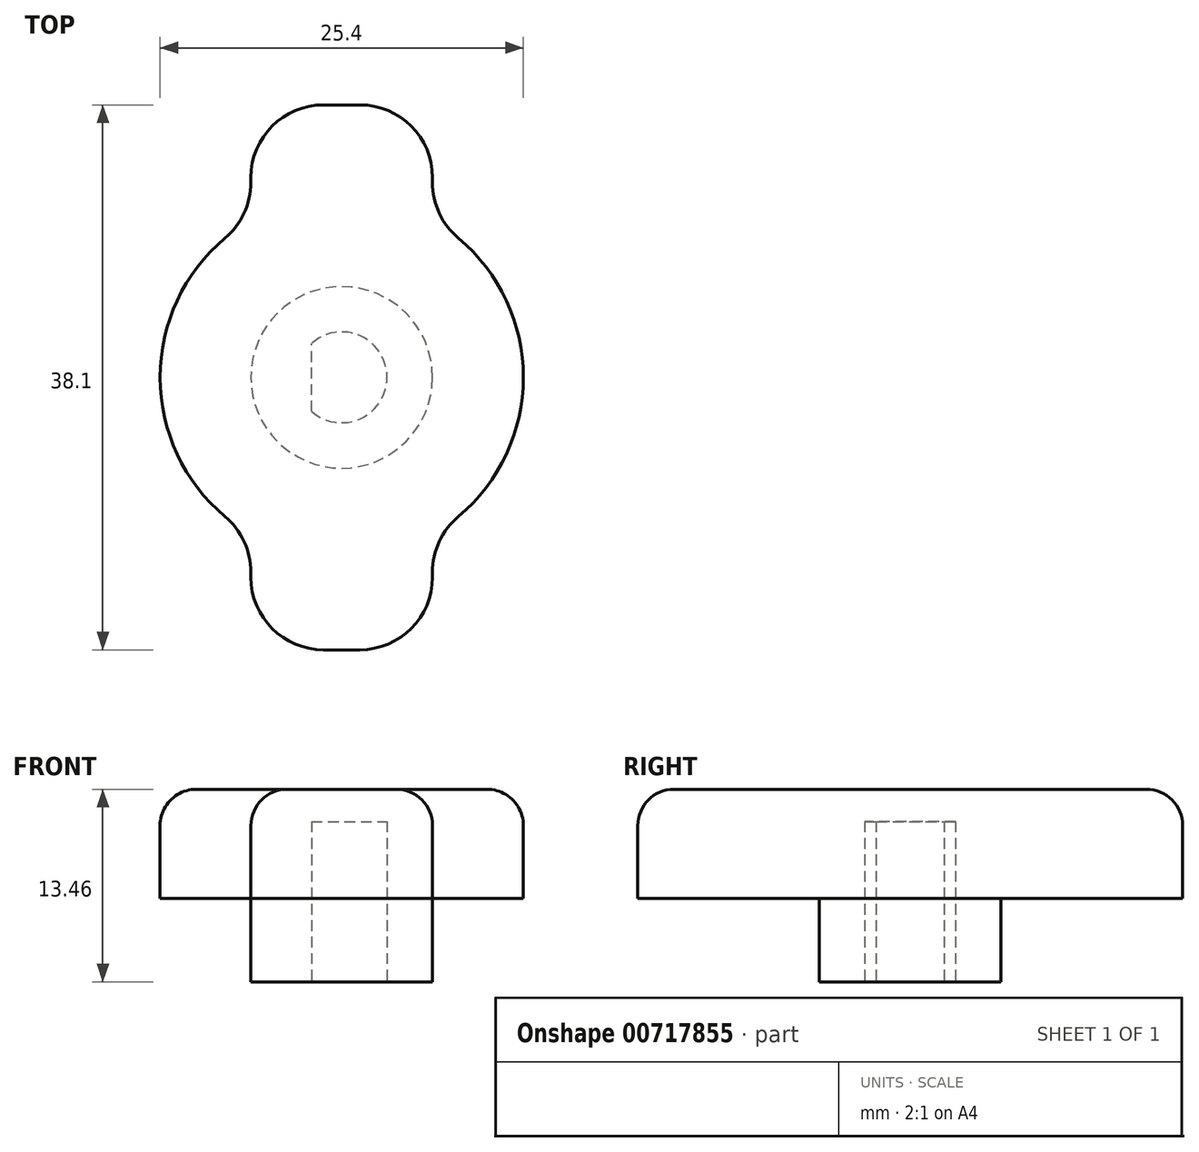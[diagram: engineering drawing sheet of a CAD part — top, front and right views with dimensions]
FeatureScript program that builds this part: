
annotation { "Feature Type Name" : "Feature", "Feature Type Description" : "" }
export const myFeature = defineFeature(function(context is Context, id is Id, definition is map)
    precondition{}
    {
        {
            var Q0;
            Q0=qCreatedBy(makeId("Top.planeOp"),FACE);
            var sketch = newSketch(context, id + "F0", { "sketchPlane" : qUnion([Q0])});
            skCircle(sketch, "E0", {"center": v(0, 0) * mm, "radius": 12.7 * mm});
            skLineSegment(sketch, "E1.bottom", {"start": v(6.35, -19.05) * mm, "end": v(-6.35, -19.05) * mm});
            skLineSegment(sketch, "E1.top", {"start": v(6.35, 19.05) * mm, "end": v(-6.35, 19.05) * mm});
            skLineSegment(sketch, "E1.left", {"start": v(6.35, -19.05) * mm, "end": v(6.35, 19.05) * mm});
            skLineSegment(sketch, "E1.right", {"start": v(-6.35, -19.05) * mm, "end": v(-6.35, 19.05) * mm});
            skSolve(sketch);
        }
        {
            var Q0;
            Q0 = qSketchRegion(id + "F0", true);
            extrude(context, id + "F1", {"entities" : qUnion([Q0]), "depth" : 7.62 * mm, "offsetDistance" : 25.4 * mm});
        }
        {
            var Q0;
            {var subQ0=sQuery(id+"F0.wireOp",EDGE,"E1.left");var subQ1=sQuery(id+"F0.wireOp",EDGE,"E0");Q0=makeQuery(id+"F1.opExtrude","SWEPT_EDGE",EDGE,{"disambiguationData":[OSD([subQ1,subQ0]),TDD([makeQuery(id+"F0.imprint","INTERSECT",VERTEX,{"disambiguationData":[OD(1.0)],"derivedFrom":[subQ1,subQ0]})])]});}
            var Q1;
            Q1=makeQuery(id+"F1.opExtrude","SWEPT_EDGE",EDGE,{"disambiguationData":[OSD([sQuery(id+"F0.wireOp",EDGE,"E1.bottom"),sQuery(id+"F0.wireOp",EDGE,"E1.left")])]});
            var Q2;
            Q2=makeQuery(id+"F1.opExtrude","SWEPT_EDGE",EDGE,{"disambiguationData":[OSD([sQuery(id+"F0.wireOp",EDGE,"E1.bottom"),sQuery(id+"F0.wireOp",EDGE,"E1.right")])]});
            var Q3;
            {var subQ0=sQuery(id+"F0.wireOp",EDGE,"E1.right");var subQ1=sQuery(id+"F0.wireOp",EDGE,"E0");Q3=makeQuery(id+"F1.opExtrude","SWEPT_EDGE",EDGE,{"disambiguationData":[OSD([subQ1,subQ0]),TDD([makeQuery(id+"F0.imprint","INTERSECT",VERTEX,{"disambiguationData":[OD(1.0)],"derivedFrom":[subQ1,subQ0]})])]});}
            var Q4;
            {var subQ0=sQuery(id+"F0.wireOp",EDGE,"E1.right");var subQ1=sQuery(id+"F0.wireOp",EDGE,"E0");Q4=makeQuery(id+"F1.opExtrude","SWEPT_EDGE",EDGE,{"disambiguationData":[OSD([subQ1,subQ0]),TDD([makeQuery(id+"F0.imprint","INTERSECT",VERTEX,{"disambiguationData":[OD(0.0)],"derivedFrom":[subQ1,subQ0]})])]});}
            var Q5;
            Q5=makeQuery(id+"F1.opExtrude","SWEPT_EDGE",EDGE,{"disambiguationData":[OSD([sQuery(id+"F0.wireOp",EDGE,"E1.top"),sQuery(id+"F0.wireOp",EDGE,"E1.right")])]});
            var Q6;
            Q6=makeQuery(id+"F1.opExtrude","SWEPT_EDGE",EDGE,{"disambiguationData":[OSD([sQuery(id+"F0.wireOp",EDGE,"E1.top"),sQuery(id+"F0.wireOp",EDGE,"E1.left")])]});
            var Q7;
            {var subQ0=sQuery(id+"F0.wireOp",EDGE,"E1.left");var subQ1=sQuery(id+"F0.wireOp",EDGE,"E0");Q7=makeQuery(id+"F1.opExtrude","SWEPT_EDGE",EDGE,{"disambiguationData":[OSD([subQ1,subQ0]),TDD([makeQuery(id+"F0.imprint","INTERSECT",VERTEX,{"disambiguationData":[OD(0.0)],"derivedFrom":[subQ1,subQ0]})])]});}
            fillet(context, id + "F2", {"entities" : qUnion([Q0, Q1, Q2, Q3, Q4, Q5, Q6, Q7]), "radius" : 5.08 * mm, "tangentPropagation" : true, "allowEdgeOverflow" : false});
        }
        {
            var Q0;
            Q0=makeQuery(id+"F1.opExtrude","CAP_FACE",FACE,{"disambiguationData":[OSD([sQuery(id+"F0.wireOp",EDGE,"E0"),sQuery(id+"F0.wireOp",EDGE,"E1.bottom"),sQuery(id+"F0.wireOp",EDGE,"E1.top"),sQuery(id+"F0.wireOp",EDGE,"E1.left"),sQuery(id+"F0.wireOp",EDGE,"E1.right")])],"isStart":false});
            fillet(context, id + "F3", {"entities" : qUnion([Q0]), "radius" : 2.54 * mm, "tangentPropagation" : true, "allowEdgeOverflow" : false});
        }
        {
            var Q0;
            Q0=makeQuery(id+"F1.opExtrude","CAP_FACE",FACE,{"disambiguationData":[OSD([sQuery(id+"F0.wireOp",EDGE,"E0"),sQuery(id+"F0.wireOp",EDGE,"E1.bottom"),sQuery(id+"F0.wireOp",EDGE,"E1.top"),sQuery(id+"F0.wireOp",EDGE,"E1.left"),sQuery(id+"F0.wireOp",EDGE,"E1.right")])],"isStart":true});
            var sketch = newSketch(context, id + "F4", { "sketchPlane" : qUnion([Q0])});
            skCircle(sketch, "E2", {"center": v(0, 0) * mm, "radius": 6.35 * mm});
            skSolve(sketch);
        }
        {
            var Q0;
            Q0 = qSketchRegion(id + "F4", true);
            extrude(context, id + "F5", {"entities" : qUnion([Q0]), "operationType" : NewBodyOperationType.ADD, "depth" : 5.84 * mm, "offsetDistance" : 25.4 * mm});
        }
        {
            var Q0;
            Q0=makeQuery(id+"F5.opExtrude","CAP_FACE",FACE,{"disambiguationData":[OSD([sQuery(id+"F4.wireOp",EDGE,"E2")])],"isStart":false});
            var sketch = newSketch(context, id + "F6", { "sketchPlane" : qUnion([Q0])});
            skArc(sketch, "E3", {"start": v(-2.1, -2.37) * mm, "mid": v(3.18, 0) * mm, "end": v(-2.1, 2.37) * mm});
            skLineSegment(sketch, "E4", {"start": v(-2.1, 2.37) * mm, "end": v(-2.1, -2.37) * mm});
            skSolve(sketch);
        }
        {
            var Q0;
            Q0=makeQuery(id+"F6.imprint","IMPRINT",FACE,{"disambiguationData":[TD([[makeQuery(id+"F6.imprint","IMPRINT",EDGE,{"derivedFrom":sQuery(id+"F6.wireOp",EDGE,"E3")}),1.0]])]});
            extrude(context, id + "F7", {"entities" : qUnion([Q0]), "operationType" : NewBodyOperationType.REMOVE, "oppositeDirection" : true, "depth" : 11.2 * mm, "offsetDistance" : 25.4 * mm});
        }
    });
